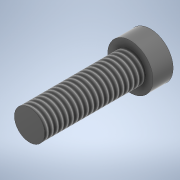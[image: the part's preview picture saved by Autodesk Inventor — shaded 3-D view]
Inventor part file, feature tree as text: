
AUTODESK INVENTOR PART (.ipt)
format: ipt  version: 2020 (Build 240168000, 168)  size: 111,104 bytes
history: native  units: in
note: dims shown in document units (in); Inventor stores cm internally (conversion verified against a paired STEP export)
features: sketch x2, extrude x2, thread x1
ambient origin geometry x8: Origin, YZ Plane, XZ Plane, XY Plane, X Axis, Y Axis, Z Axis, Center Point
bodies: Solid1 (feature_tree)
feature tree (5):
  sketch  "Sketch1"  dims[d0=0.1181in d1=0.1772in]
  extrude  "Extrusion1"  Depth=0.1772in
  extrude  "Extrusion2"  Depth=0.3937in TaperAngle=0.0deg
  thread  "Thread1"  [1 undecoded]
  sketch  "Sketch2"  dims[d2=0.1181in d3=0.1772in d4=0.3937in d5=0.0in d6=0.0787in d7=0.0in d8=0.3937in d9=0.0in]
note: 1 required parameter value undecoded (feature->parameter linkage not recoverable at this tier; creation-order binding heuristic only, values carry confidence <= 0.55)
